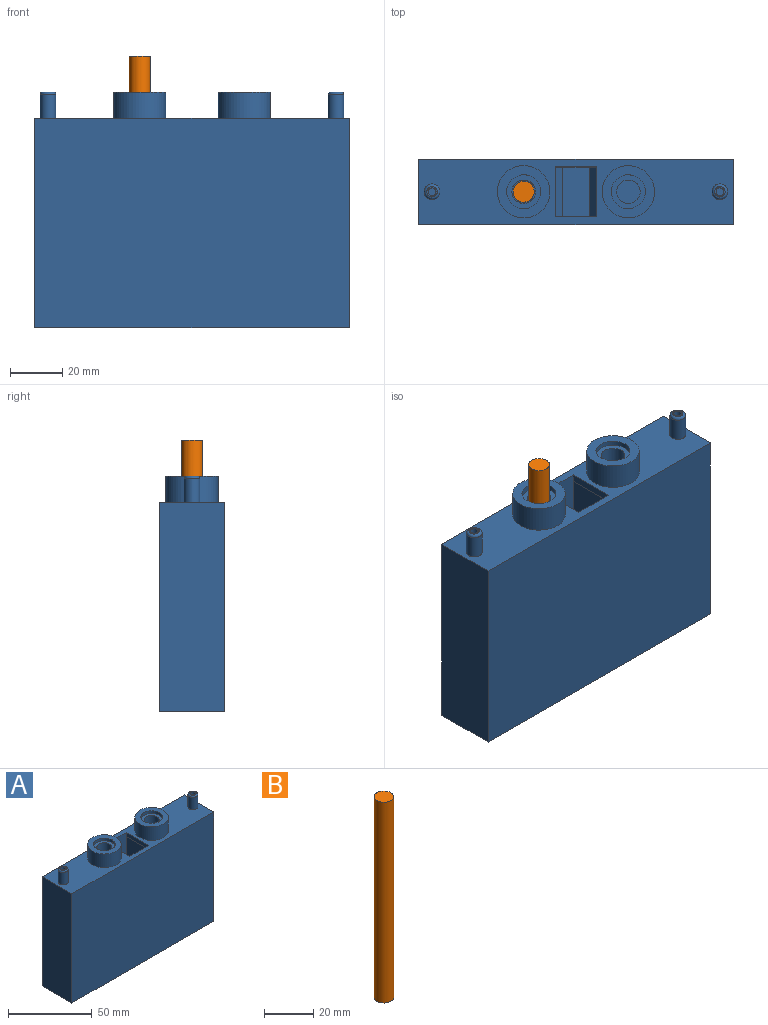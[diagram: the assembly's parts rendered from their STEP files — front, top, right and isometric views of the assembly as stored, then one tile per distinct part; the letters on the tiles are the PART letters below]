
ASSEMBLY  parts=2 mates=1
PART A: 93 faces, bbox 120x25x90 mm
  f0: cylinder r=4.5mm len=11mm, axis (0,0,1), area 311mm2, adj f23,f91
  f1: cylinder r=4.5mm len=11mm, axis (0,0,1), area 311mm2, adj f2,f90
  f2: plane 49x19mm, normal (0,0,-1), area 860.3mm2, adj f1,f3,f4,f33,f70,f72
  f3: plane 114x77mm, normal (0,-1,0), area 8208.3mm2, adj f2,f5,f6,f7,f8,f9,f10,f11
  f4: plane 114x77mm, normal (0,1,0), area 8208.3mm2, adj f2,f5,f6,f7,f8,f9,f10,f11
  f5: plane 19x7.14mm, normal (0.82,0,0.57), area 165.6mm2, adj f3,f4,f29,f30
  f6: plane 19x7.14mm, normal (0.82,0,0.57), area 165.6mm2, adj f3,f4,f66,f67
  f7: plane 19x7.14mm, normal (0.82,0,0.57), area 165.6mm2, adj f3,f4,f63,f64
  f8: plane 19x7.14mm, normal (0.82,0,0.57), area 165.6mm2, adj f3,f4,f60,f61
  f9: plane 19x7.14mm, normal (0.82,0,0.57), area 165.6mm2, adj f3,f4,f57,f58
  f10: plane 19x7.14mm, normal (0.82,0,0.57), area 165.6mm2, adj f3,f4,f54,f55
  f11: plane 19x3mm, normal (1,0,0), area 57mm2, adj f3,f4,f24,f52
  f12: plane 19x3mm, normal (-1,0,0), area 57mm2, adj f3,f4,f49,f50
  f13: plane 19x3mm, normal (-1,0,0), area 57mm2, adj f3,f4,f46,f47
  f14: plane 19x3mm, normal (1,0,0), area 57mm2, adj f3,f4,f25,f44
  f15: plane 19x7.14mm, normal (-0.82,0,0.57), area 165.6mm2, adj f3,f4,f26,f42
  f16: plane 19x3mm, normal (-1,0,0), area 57mm2, adj f3,f4,f39,f40
  f17: plane 19x2mm, normal (0,0,1), area 38mm2, adj f3,f4,f18,f27
  f18: plane 19x17.99mm, normal (1,0,0), area 341.8mm2, adj f3,f4,f17,f19
  f19: plane 19x7.14mm, normal (0.82,0,-0.57), area 165.6mm2, adj f3,f4,f18,f37
  f20: plane 19x17.85mm, normal (1,0,0), area 339.1mm2, adj f3,f4,f21,f28
  f21: plane 19x4.28mm, normal (0.82,0,0.57), area 99.4mm2, adj f3,f4,f20,f22
  f22: plane 19x3mm, normal (1,0,0), area 57mm2, adj f3,f4,f21,f35
  f23: plane 49x19mm, normal (0,0,-1), area 860.3mm2, adj f0,f3,f4,f32,f69,f71
  f24: plane 19x7.14mm, normal (-0.82,0,0.57), area 165.6mm2, adj f3,f4,f11,f53
  f25: plane 19x7.14mm, normal (-0.82,0,0.57), area 165.6mm2, adj f3,f4,f14,f45
  f26: plane 19x3mm, normal (-1,0,0), area 57mm2, adj f3,f4,f15,f43
  f27: plane 19x17.85mm, normal (-1,0,0), area 339.1mm2, adj f3,f4,f17,f38
  f28: plane 19x2mm, normal (0,0,1), area 38mm2, adj f3,f4,f20,f36
  f29: plane 19x3mm, normal (1,0,0), area 57mm2, adj f3,f4,f5,f31
  f30: plane 19x3mm, normal (-1,0,0), area 57mm2, adj f3,f4,f5,f31
  f31: plane 19x7.14mm, normal (-0.82,0,-0.57), area 165.6mm2, adj f3,f4,f29,f30
  f32: plane 74x19mm, normal (1,0,0), area 1406mm2, adj f3,f4,f23,f34
  f33: plane 74x19mm, normal (-1,0,0), area 1406mm2, adj f2,f3,f4,f34
  f34: plane 114x19mm, normal (0,0,1), area 2166mm2, adj f3,f4,f32,f33
  f35: plane 19x7.14mm, normal (-0.82,0,-0.57), area 165.6mm2, adj f3,f4,f22,f36
  f36: plane 19x17.99mm, normal (-1,0,0), area 341.8mm2, adj f3,f4,f28,f35
  f37: plane 19x3mm, normal (-1,0,0), area 57mm2, adj f3,f4,f19,f38
  f38: plane 19x4.28mm, normal (-0.82,0,0.57), area 99.4mm2, adj f3,f4,f27,f37
  f39: plane 19x7.14mm, normal (-0.82,0,0.57), area 165.6mm2, adj f3,f4,f16,f41
  f40: plane 19x7.14mm, normal (0.82,0,-0.57), area 165.6mm2, adj f3,f4,f16,f41
  f41: plane 19x3mm, normal (1,0,0), area 57mm2, adj f3,f4,f39,f40
  f42: plane 19x3mm, normal (1,0,0), area 57mm2, adj f3,f4,f15,f43
  f43: plane 19x7.14mm, normal (0.82,0,-0.57), area 165.6mm2, adj f3,f4,f26,f42
  f44: plane 19x7.14mm, normal (0.82,0,-0.57), area 165.6mm2, adj f3,f4,f14,f45
  f45: plane 19x3mm, normal (-1,0,0), area 57mm2, adj f3,f4,f25,f44
  f46: plane 19x7.14mm, normal (-0.82,0,0.57), area 165.6mm2, adj f3,f4,f13,f48
  f47: plane 19x7.14mm, normal (0.82,0,-0.57), area 165.6mm2, adj f3,f4,f13,f48
  f48: plane 19x3mm, normal (1,0,0), area 57mm2, adj f3,f4,f46,f47
  f49: plane 19x7.14mm, normal (-0.82,0,0.57), area 165.6mm2, adj f3,f4,f12,f51
  f50: plane 19x7.14mm, normal (0.82,0,-0.57), area 165.6mm2, adj f3,f4,f12,f51
  f51: plane 19x3mm, normal (1,0,0), area 57mm2, adj f3,f4,f49,f50
  f52: plane 19x7.14mm, normal (0.82,0,-0.57), area 165.6mm2, adj f3,f4,f11,f53
  f53: plane 19x3mm, normal (-1,0,0), area 57mm2, adj f3,f4,f24,f52
  f54: plane 19x3mm, normal (1,0,0), area 57mm2, adj f3,f4,f10,f56
  f55: plane 19x3mm, normal (-1,0,0), area 57mm2, adj f3,f4,f10,f56
  f56: plane 19x7.14mm, normal (-0.82,0,-0.57), area 165.6mm2, adj f3,f4,f54,f55
  f57: plane 19x3mm, normal (1,0,0), area 57mm2, adj f3,f4,f9,f59
  f58: plane 19x3mm, normal (-1,0,0), area 57mm2, adj f3,f4,f9,f59
  f59: plane 19x7.14mm, normal (-0.82,0,-0.57), area 165.6mm2, adj f3,f4,f57,f58
  f60: plane 19x3mm, normal (1,0,0), area 57mm2, adj f3,f4,f8,f62
  f61: plane 19x3mm, normal (-1,0,0), area 57mm2, adj f3,f4,f8,f62
  f62: plane 19x7.14mm, normal (-0.82,0,-0.57), area 165.6mm2, adj f3,f4,f60,f61
  f63: plane 19x3mm, normal (1,0,0), area 57mm2, adj f3,f4,f7,f65
  f64: plane 19x3mm, normal (-1,0,0), area 57mm2, adj f3,f4,f7,f65
  f65: plane 19x7.14mm, normal (-0.82,0,-0.57), area 165.6mm2, adj f3,f4,f63,f64
  f66: plane 19x3mm, normal (1,0,0), area 57mm2, adj f3,f4,f6,f68
  f67: plane 19x3mm, normal (-1,0,0), area 57mm2, adj f3,f4,f6,f68
  f68: plane 19x7.14mm, normal (-0.82,0,-0.57), area 165.6mm2, adj f3,f4,f66,f67
  f69: plane 19x3mm, normal (1,0,0), area 57mm2, adj f3,f4,f23,f73
  f70: plane 19x3mm, normal (-1,0,0), area 57mm2, adj f2,f3,f4,f73
  f71: cylinder r=1.5mm len=13mm, axis (0,0,1), area 122.5mm2, adj f23,f82
  f72: cylinder r=1.5mm len=13mm, axis (0,0,1), area 122.5mm2, adj f2,f86
  f73: plane 120x25mm, normal (0,0,1), area 2011.1mm2, adj f3,f4,f69,f70,f74,f76,f77,f78
  f74: plane 80x25mm, normal (-1,0,0), area 2000mm2, adj f73,f75,f77,f78
  f75: plane 120x25mm, normal (0,0,-1), area 3000mm2, adj f74,f76,f77,f78
  f76: plane 80x25mm, normal (1,0,0), area 2000mm2, adj f73,f75,f77,f78
  f77: plane 120x80mm, normal (0,-1,0), area 9600mm2, adj f73,f74,f75,f76
  f78: plane 120x80mm, normal (0,1,0), area 9600mm2, adj f73,f74,f75,f76
  f79: cylinder r=10mm len=20mm, axis (0,0,-1), area 628.3mm2, adj f73,f80
  f80: plane 20x20mm, normal (0,0,1), area 181.4mm2, adj f79,f92
  f81: cylinder r=3mm len=9mm, axis (0,0,-1), area 169.6mm2, adj f73,f88
  f82: plane 4x4mm, normal (0,0,1), area 5.5mm2, adj f71,f88
  f83: cylinder r=10mm len=20mm, axis (0,0,-1), area 628.3mm2, adj f73,f84
  f84: plane 20x20mm, normal (0,0,1), area 181.4mm2, adj f83,f89
  f85: cylinder r=3mm len=9mm, axis (0,0,-1), area 169.6mm2, adj f73,f87
  f86: plane 4x4mm, normal (0,0,1), area 5.5mm2, adj f72,f87
  f87: torus R=2mm, axis (0,0,1), area 26mm2, adj f85,f86
  f88: torus R=2mm, axis (0,0,1), area 26mm2, adj f81,f82
  f89: cylinder r=6.5mm len=13mm, axis (0,0,1), area 81.7mm2, adj f84,f90
  f90: plane 13x13mm, normal (0,0,1), area 69.1mm2, adj f1,f89
  f91: plane 13x13mm, normal (0,0,1), area 69.1mm2, adj f0,f92
  f92: cylinder r=6.5mm len=13mm, axis (0,0,1), area 81.7mm2, adj f80,f91
PART B: 3 faces, bbox 8x8x100 mm
  f0: cylinder r=4mm len=100mm, axis (0,0,-1), area 2513.3mm2, adj f1,f2
  f1: plane 8x8mm, normal (0,0,1), area 50.3mm2, adj f0
  f2: plane 8x8mm, normal (0,0,-1), area 50.3mm2, adj f0
PLACE A t=(-60,12.5,0)mm
PLACE B t=(-20,0,-76.4)mm
MATE slider B.f0 <-> A.f0  axis (0,0,-1) through (-20,0,-76.4)mm
